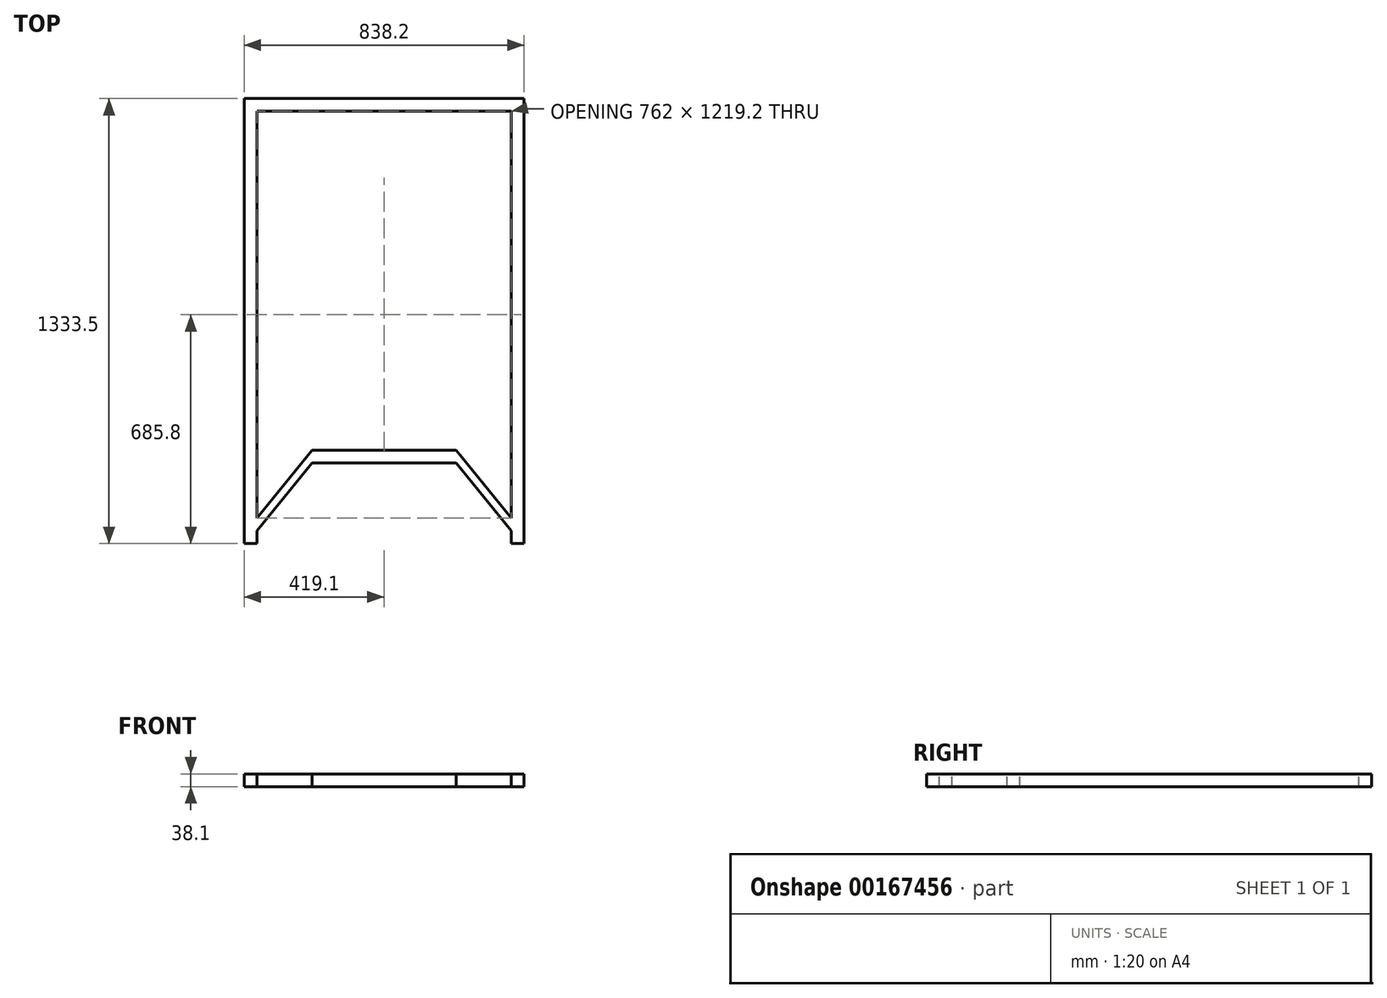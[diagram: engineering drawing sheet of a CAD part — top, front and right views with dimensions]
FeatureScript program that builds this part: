
annotation { "Feature Type Name" : "Feature", "Feature Type Description" : "" }
export const myFeature = defineFeature(function(context is Context, id is Id, definition is map)
    precondition{}
    {
        {
            var Q0;
            Q0=qCreatedBy(makeId("Top.planeOp"),FACE);
            var sketch = newSketch(context, id + "F0", { "sketchPlane" : qUnion([Q0])});
            skLineSegment(sketch, "E0.bottom", {"start": v(-419.1, 666.75) * mm, "end": v(419.1, 666.75) * mm});
            skLineSegment(sketch, "E0.left", {"start": v(-419.1, 666.75) * mm, "end": v(-419.1, -666.75) * mm});
            skLineSegment(sketch, "E0.right", {"start": v(419.1, 666.75) * mm, "end": v(419.1, -666.75) * mm});
            skPoint(sketch, "E0.middle", {"position": v(0, 0) * mm});
            skLineSegment(sketch, "E1.bottom", {"start": v(-381, 628.65) * mm, "end": v(381, 628.65) * mm});
            skLineSegment(sketch, "E1.left", {"start": v(-381, 628.65) * mm, "end": v(-381, -628.65) * mm});
            skLineSegment(sketch, "E1.right", {"start": v(381, 628.65) * mm, "end": v(381, -628.65) * mm});
            skLineSegment(sketch, "E2", {"start": v(-215.9, -425.45) * mm, "end": v(215.9, -425.45) * mm});
            skLineSegment(sketch, "E3", {"start": v(215.9, -425.45) * mm, "end": v(381, -628.65) * mm});
            skLineSegment(sketch, "E4", {"start": v(-215.9, -425.45) * mm, "end": v(-381, -628.65) * mm});
            skLineSegment(sketch, "E5", {"start": v(-215.9, -387.35) * mm, "end": v(215.9, -387.35) * mm});
            skLineSegment(sketch, "E6", {"start": v(-215.9, -387.35) * mm, "end": v(-381, -590.55) * mm});
            skLineSegment(sketch, "E7", {"start": v(215.9, -387.35) * mm, "end": v(381, -590.55) * mm});
            skLineSegment(sketch, "E8", {"start": v(-419.1, -666.75) * mm, "end": v(-381, -666.75) * mm});
            skLineSegment(sketch, "E9", {"start": v(-381, -666.75) * mm, "end": v(-381, -628.65) * mm});
            skLineSegment(sketch, "E10", {"start": v(419.1, -666.75) * mm, "end": v(381, -666.75) * mm});
            skLineSegment(sketch, "E11", {"start": v(381, -666.75) * mm, "end": v(381, -628.65) * mm});
            skSolve(sketch);
        }
        {
            var Q0;
            Q0=makeQuery(id+"F0.imprint","IMPRINT",FACE,{"disambiguationData":[TD([[makeQuery(id+"F0.imprint","IMPRINT",EDGE,{"derivedFrom":sQuery(id+"F0.wireOp",EDGE,"E2")}),1.0]])]});
            var Q1;
            Q1=makeQuery(id+"F0.imprint","IMPRINT",FACE,{"disambiguationData":[TD([[makeQuery(id+"F0.imprint","IMPRINT",EDGE,{"derivedFrom":sQuery(id+"F0.wireOp",EDGE,"E0.bottom")}),-1.0]])]});
            extrude(context, id + "F1", {"entities" : qUnion([Q0, Q1]), "oppositeDirection" : true, "depth" : 38.1 * mm});
        }
    });
